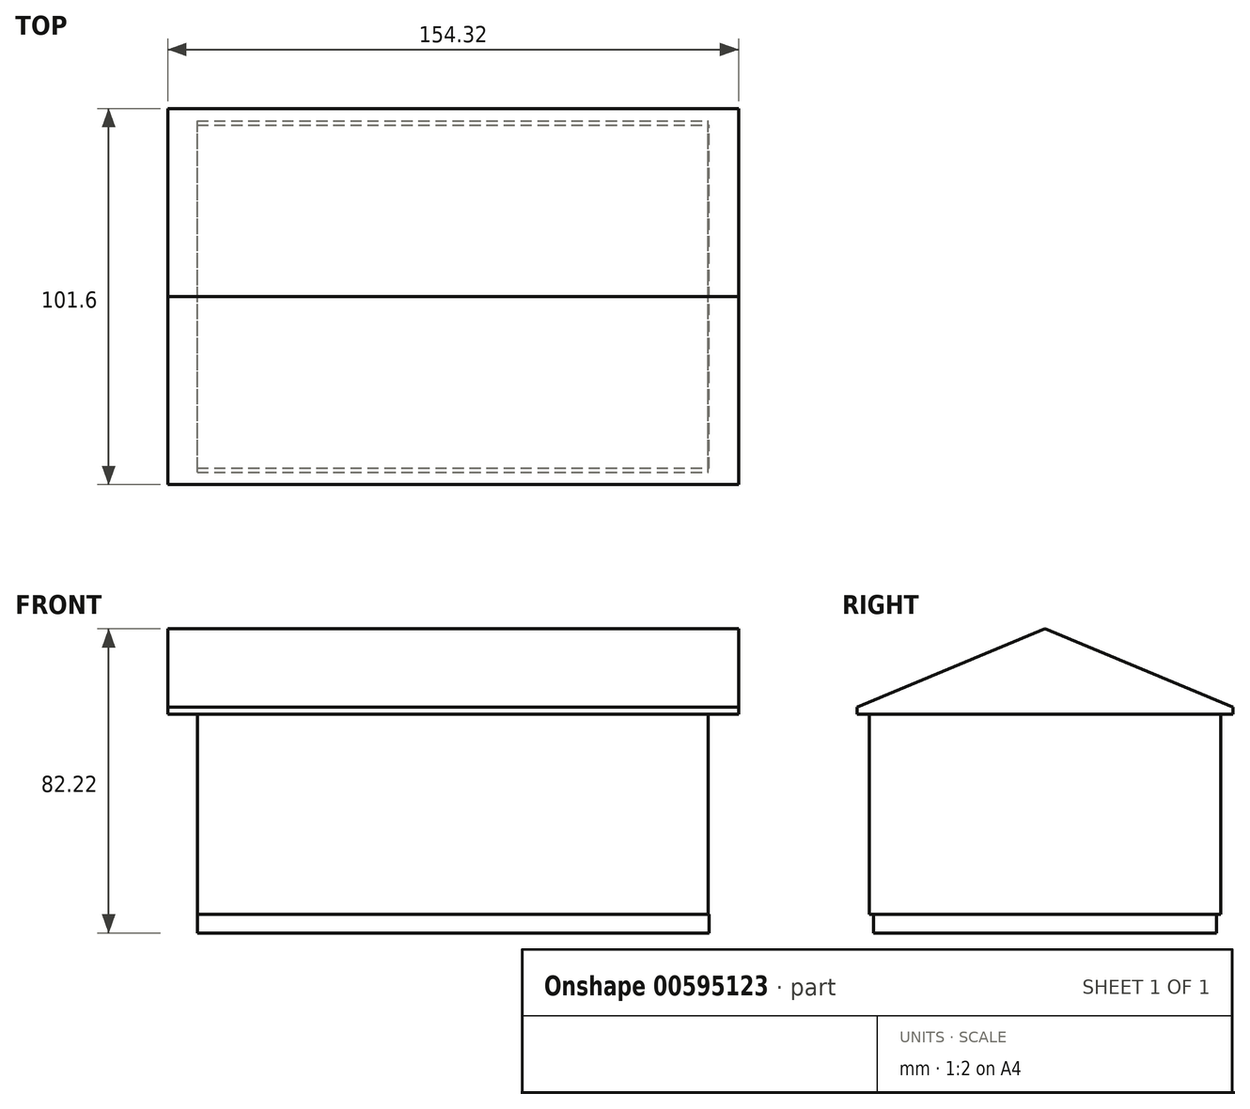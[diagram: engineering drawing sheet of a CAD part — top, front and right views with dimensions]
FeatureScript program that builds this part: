
annotation { "Feature Type Name" : "Feature", "Feature Type Description" : "" }
export const myFeature = defineFeature(function(context is Context, id is Id, definition is map)
    precondition{}
    {
        {
            var Q0;
            Q0=qCreatedBy(makeId("Front.planeOp"),FACE);
            var sketch = newSketch(context, id + "F0", { "sketchPlane" : qUnion([Q0])});
            skLineSegment(sketch, "E0.bottom", {"start": v(-69.07, 30.48) * mm, "end": v(69.07, 30.48) * mm});
            skLineSegment(sketch, "E0.top", {"start": v(-69.07, -30.48) * mm, "end": v(69.07, -30.48) * mm});
            skLineSegment(sketch, "E0.left", {"start": v(-69.07, 30.48) * mm, "end": v(-69.07, -30.48) * mm});
            skLineSegment(sketch, "E0.right", {"start": v(69.07, 30.48) * mm, "end": v(69.07, -30.48) * mm});
            skPoint(sketch, "E0.middle", {"position": v(0, 0) * mm});
            skLineSegment(sketch, "E1.bottom", {"start": v(-77.06, 23.69) * mm, "end": v(77.26, 23.69) * mm});
            skLineSegment(sketch, "E1.top", {"start": v(-77.06, 56.07) * mm, "end": v(77.26, 56.07) * mm});
            skLineSegment(sketch, "E1.left", {"start": v(-77.06, 23.69) * mm, "end": v(-77.06, 56.07) * mm});
            skLineSegment(sketch, "E1.right", {"start": v(77.26, 23.69) * mm, "end": v(77.26, 56.07) * mm});
            skLineSegment(sketch, "E2.bottom", {"start": v(-69.07, -30.48) * mm, "end": v(69.27, -30.48) * mm});
            skLineSegment(sketch, "E2.top", {"start": v(-69.07, -35.48) * mm, "end": v(69.27, -35.48) * mm});
            skLineSegment(sketch, "E2.left", {"start": v(-69.07, -30.48) * mm, "end": v(-69.07, -35.48) * mm});
            skLineSegment(sketch, "E2.right", {"start": v(69.27, -30.48) * mm, "end": v(69.27, -35.48) * mm});
            skSolve(sketch);
        }
        {
            var Q0;
            {var subQ0=sQuery(id+"F0.wireOp",EDGE,"E2.bottom");var subQ5=sQuery(id+"F0.wireOp",EDGE,"E0.right");var subQ6=makeQuery(id+"F0.imprint","INTERSECT",VERTEX,{"derivedFrom":[subQ5,subQ0]});Q0=makeQuery(id+"F0.imprint","IMPRINT",FACE,{"disambiguationData":[TD([[makeQuery(id+"F0.imprint","IMPRINT",EDGE,{"disambiguationData":[TD([[subQ6,1.0]])],"derivedFrom":subQ5}),-1.0]])]});}
            extrude(context, id + "F1", {"entities" : qUnion([Q0]), "endBound" : BoundingType.SYMMETRIC, "depth" : 95 * mm, "offsetDistance" : 25.4 * mm});
        }
        {
            var Q0;
            {var subQ0=sQuery(id+"F0.wireOp",EDGE,"E0.bottom");Q0=makeQuery(id+"F0.imprint","IMPRINT",FACE,{"disambiguationData":[TD([[makeQuery(id+"F0.imprint","IMPRINT",EDGE,{"derivedFrom":subQ0}),-1.0]])]});}
            var Q1;
            {var subQ1=sQuery(id+"F0.wireOp",EDGE,"E0.bottom");Q1=makeQuery(id+"F0.imprint","IMPRINT",FACE,{"disambiguationData":[TD([[makeQuery(id+"F0.imprint","IMPRINT",EDGE,{"derivedFrom":subQ1}),1.0]])]});}
            var Q2;
            Q2=sQuery(id+"F0.wireOp",EDGE,"E1.right");
            var Q3;
            Q3=sQuery(id+"F0.wireOp",EDGE,"E1.bottom");
            var Q4;
            Q4=sQuery(id+"F0.wireOp",EDGE,"E1.top");
            var Q5;
            Q5=sQuery(id+"F0.wireOp",EDGE,"E1.left");
            extrude(context, id + "F2", {"entities" : qUnion([Q0, Q1]), "surfaceEntities" : qUnion([Q2, Q3, Q4, Q5]), "endBound" : BoundingType.SYMMETRIC, "depth" : 101.6 * mm, "offsetDistance" : 25.4 * mm});
        }
        {
            var Q0;
            Q0=makeQuery(id+"F2.opExtrude","CAP_EDGE",EDGE,{"disambiguationData":[OSD([sQuery(id+"F0.wireOp",EDGE,"E1.top")])],"isStart":true});
            var Q1;
            Q1=makeQuery(id+"F2.opExtrude","CAP_EDGE",EDGE,{"disambiguationData":[OSD([sQuery(id+"F0.wireOp",EDGE,"E1.top")])],"isStart":false});
            chamfer(context, id + "F3", {"entities" : qUnion([Q0, Q1]), "chamferType" : ChamferType.OFFSET_ANGLE, "width" : 30.48 * mm, "oppositeDirection" : false, "angle" : 67.4 * degree, "tangentPropagation" : true});
        }
        {
            var Q0;
            Q0=makeQuery(id+"F0.imprint","IMPRINT",FACE,{"disambiguationData":[TD([[makeQuery(id+"F0.imprint","IMPRINT",EDGE,{"derivedFrom":sQuery(id+"F0.wireOp",EDGE,"E2.top")}),1.0]])]});
            extrude(context, id + "F4", {"entities" : qUnion([Q0]), "operationType" : NewBodyOperationType.ADD, "endBound" : BoundingType.SYMMETRIC, "depth" : 92.7 * mm, "offsetDistance" : 25.4 * mm});
        }
    });
